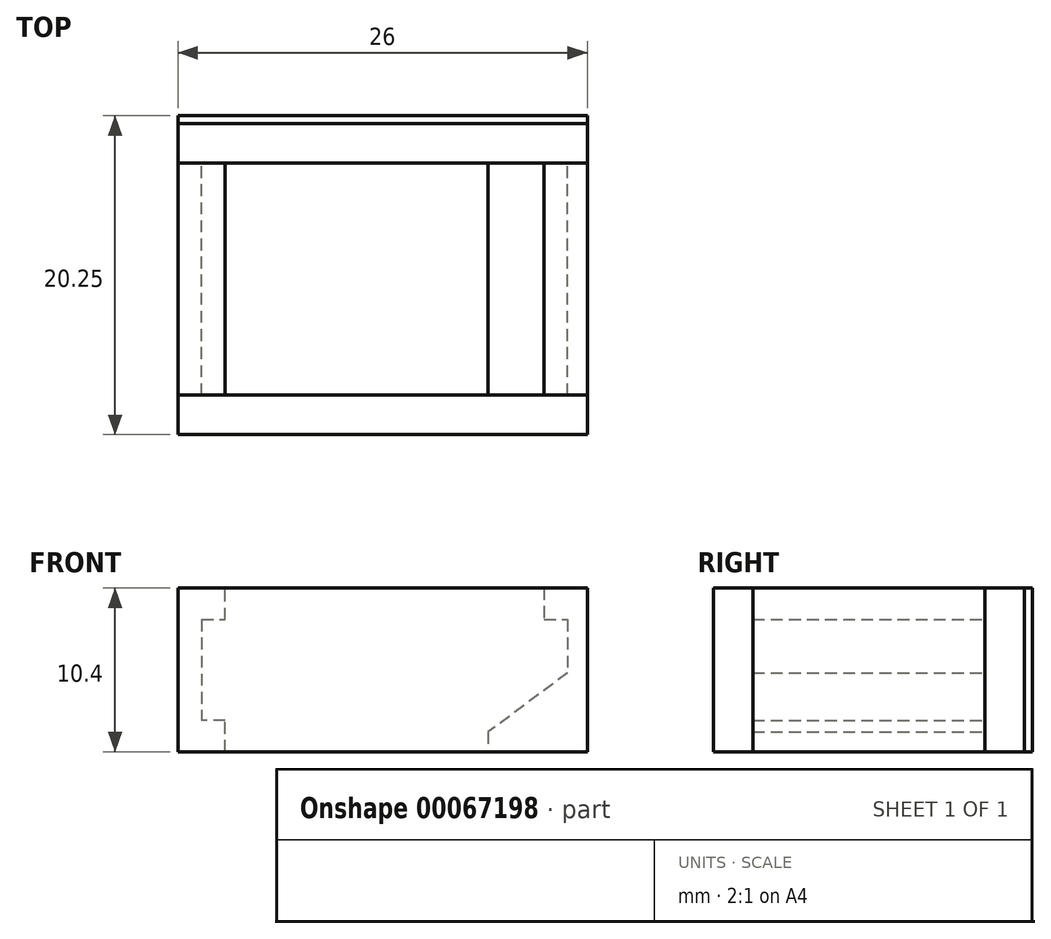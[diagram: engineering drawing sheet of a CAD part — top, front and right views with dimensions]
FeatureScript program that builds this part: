
annotation { "Feature Type Name" : "Feature", "Feature Type Description" : "" }
export const myFeature = defineFeature(function(context is Context, id is Id, definition is map)
    precondition{}
    {
        {
            var Q0;
            Q0=qCreatedBy(makeId("Front.planeOp"),FACE);
            var sketch = newSketch(context, id + "F0", { "sketchPlane" : qUnion([Q0])});
            skLineSegment(sketch, "E0", {"start": v(0, 10.4) * mm, "end": v(0, 0) * mm});
            skLineSegment(sketch, "E1", {"start": v(0, 0) * mm, "end": v(26, 0) * mm});
            skLineSegment(sketch, "E2", {"start": v(26, 0) * mm, "end": v(26, 10.4) * mm});
            skLineSegment(sketch, "E3", {"start": v(26, 10.4) * mm, "end": v(0, 10.4) * mm});
            skLineSegment(sketch, "E4", {"start": v(3, 0) * mm, "end": v(3, 2) * mm});
            skLineSegment(sketch, "E5", {"start": v(1.5, 8.4) * mm, "end": v(3, 8.4) * mm});
            skLineSegment(sketch, "E6", {"start": v(23.25, 8.4) * mm, "end": v(24.75, 8.4) * mm});
            skPoint(sketch, "E6.startSnap0", {"position": v(13, 0) * mm});
            skLineSegment(sketch, "E7", {"start": v(23.25, 10.4) * mm, "end": v(23.25, 8.4) * mm});
            skLineSegment(sketch, "E8", {"start": v(19.7, 1.25) * mm, "end": v(19.7, 0) * mm});
            skPoint(sketch, "E9.orphan", {"position": v(13, 8.4) * mm});
            skLineSegment(sketch, "E10", {"start": v(3, 2) * mm, "end": v(1.5, 2) * mm});
            skLineSegment(sketch, "E11", {"start": v(1.5, 8.4) * mm, "end": v(1.5, 2) * mm});
            skLineSegment(sketch, "E12.trimOffspring", {"start": v(3, 8.4) * mm, "end": v(3, 10.4) * mm});
            skLineSegment(sketch, "E13", {"start": v(24.75, 8.4) * mm, "end": v(24.75, 5) * mm});
            skLineSegment(sketch, "E14", {"start": v(24.75, 5) * mm, "end": v(19.7, 1.25) * mm});
            skSolve(sketch);
        }
        {
            var Q0;
            {var subQ2=sQuery(id+"F0.wireOp",EDGE,"E0");Q0=makeQuery(id+"F0.imprint","IMPRINT",FACE,{"disambiguationData":[TD([[makeQuery(id+"F0.imprint","IMPRINT",EDGE,{"derivedFrom":subQ2}),1.0]])]});}
            var Q1;
            {var subQ0=sQuery(id+"F0.wireOp",EDGE,"E2");Q1=makeQuery(id+"F0.imprint","IMPRINT",FACE,{"disambiguationData":[TD([[makeQuery(id+"F0.imprint","IMPRINT",EDGE,{"derivedFrom":subQ0}),1.0]])]});}
            extrude(context, id + "F1", {"entities" : qUnion([Q0, Q1]), "depth" : 14.75 * mm});
        }
        {
            var Q0;
            {var subQ1=sQuery(id+"F0.wireOp",EDGE,"E4");Q0=makeQuery(id+"F0.imprint","IMPRINT",FACE,{"disambiguationData":[TD([[makeQuery(id+"F0.imprint","IMPRINT",EDGE,{"derivedFrom":subQ1}),-1.0]])]});}
            var Q1;
            {var subQ0=sQuery(id+"F0.wireOp",EDGE,"E2");Q1=makeQuery(id+"F0.imprint","IMPRINT",FACE,{"disambiguationData":[TD([[makeQuery(id+"F0.imprint","IMPRINT",EDGE,{"derivedFrom":subQ0}),1.0]])]});}
            var Q2;
            {var subQ2=sQuery(id+"F0.wireOp",EDGE,"E0");Q2=makeQuery(id+"F0.imprint","IMPRINT",FACE,{"disambiguationData":[TD([[makeQuery(id+"F0.imprint","IMPRINT",EDGE,{"derivedFrom":subQ2}),1.0]])]});}
            extrude(context, id + "F2", {"entities" : qUnion([Q0, Q1, Q2]), "oppositeDirection" : true, "depth" : 3 * mm});
        }
        {
            var Q0;
            Q0=makeQuery(id+"F1.opExtrude","CAP_FACE",FACE,{"disambiguationData":[OSD([sQuery(id+"F0.wireOp",EDGE,"E0"),sQuery(id+"F0.wireOp",EDGE,"E1"),sQuery(id+"F0.wireOp",EDGE,"E3"),sQuery(id+"F0.wireOp",EDGE,"E4"),sQuery(id+"F0.wireOp",EDGE,"E5"),sQuery(id+"F0.wireOp",EDGE,"E10"),sQuery(id+"F0.wireOp",EDGE,"E11"),sQuery(id+"F0.wireOp",EDGE,"E12.trimOffspring")])],"isStart":false});
            var sketch = newSketch(context, id + "F3", { "sketchPlane" : qUnion([Q0])});
            skLineSegment(sketch, "E15.0", {"start": v(0, 10.4) * mm, "end": v(0, 0) * mm});
            skLineSegment(sketch, "E16.0", {"start": v(26, 0) * mm, "end": v(26, 10.4) * mm});
            skLineSegment(sketch, "E17", {"start": v(0, 10.4) * mm, "end": v(26, 10.4) * mm});
            skLineSegment(sketch, "E18", {"start": v(0, 0) * mm, "end": v(26, 0) * mm});
            skSolve(sketch);
        }
        {
            var Q0;
            Q0 = qSketchRegion(id + "F3", true);
            extrude(context, id + "F4", {"entities" : qUnion([Q0]), "depth" : 2.5 * mm});
        }
        {
            var Q0;
            Q0=qCreatedBy(makeId("Front.planeOp"),FACE);
            var sketch = newSketch(context, id + "F5", { "sketchPlane" : qUnion([Q0])});
            skLineSegment(sketch, "E19.1", {"start": v(0, 10.4) * mm, "end": v(0, 0) * mm});
            skLineSegment(sketch, "E20.0", {"start": v(26, 0) * mm, "end": v(26, 10.4) * mm});
            skLineSegment(sketch, "E21", {"start": v(26, 10.4) * mm, "end": v(0, 10.4) * mm});
            skLineSegment(sketch, "E22", {"start": v(26, 0) * mm, "end": v(0, 0) * mm});
            skSolve(sketch);
        }
        {
            var Q0;
            Q0 = qSketchRegion(id + "F5", true);
            extrude(context, id + "F6", {"entities" : qUnion([Q0]), "oppositeDirection" : true, "depth" : 2.5 * mm});
        }
    });
